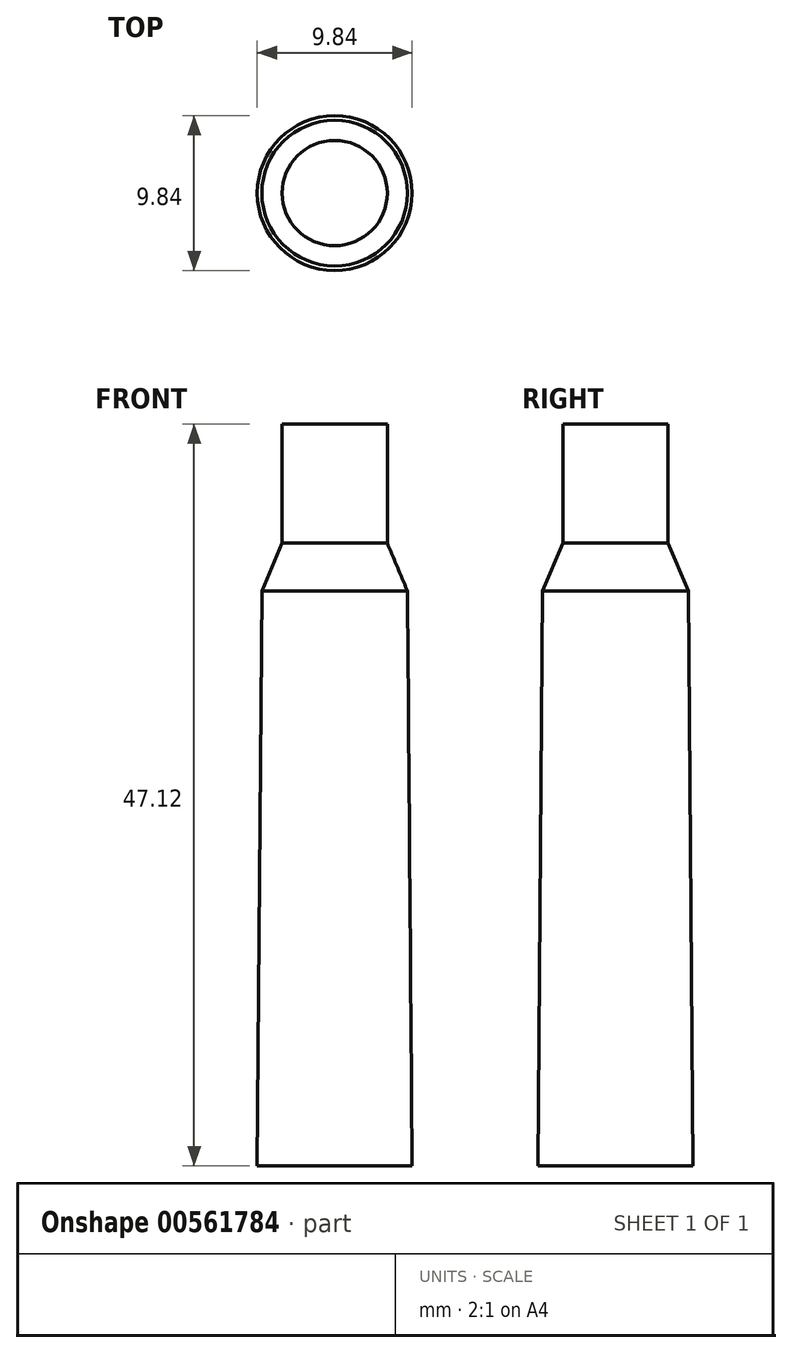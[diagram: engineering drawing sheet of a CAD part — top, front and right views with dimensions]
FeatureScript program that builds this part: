
annotation { "Feature Type Name" : "Feature", "Feature Type Description" : "" }
export const myFeature = defineFeature(function(context is Context, id is Id, definition is map)
    precondition{}
    {
        {
            var Q0;
            Q0=qCreatedBy(makeId("Front.planeOp"),FACE);
            var sketch = newSketch(context, id + "F0", { "sketchPlane" : qUnion([Q0])});
            skLineSegment(sketch, "E0", {"start": v(0, 0) * mm, "end": v(4.92, 0) * mm});
            skLineSegment(sketch, "E1", {"start": v(4.92, 0) * mm, "end": v(4.63, 36.52) * mm});
            skLineSegment(sketch, "E2", {"start": v(4.63, 36.52) * mm, "end": v(0, 36.52) * mm, "construction": true});
            skLineSegment(sketch, "E3", {"start": v(0, 39.55) * mm, "end": v(3.34, 39.55) * mm, "construction": true});
            skLineSegment(sketch, "E4", {"start": v(0, 47.12) * mm, "end": v(3.34, 47.12) * mm});
            skLineSegment(sketch, "E5", {"start": v(3.34, 47.12) * mm, "end": v(3.34, 39.55) * mm});
            skLineSegment(sketch, "E6", {"start": v(4.63, 36.52) * mm, "end": v(3.34, 39.55) * mm});
            skLineSegment(sketch, "E7.MirrorCS", {"start": v(-4.63, 36.52) * mm, "end": v(-3.34, 39.55) * mm});
            skLineSegment(sketch, "E8.MirrorCS", {"start": v(-3.34, 47.12) * mm, "end": v(-3.34, 39.55) * mm});
            skLineSegment(sketch, "E9.MirrorCS", {"start": v(-4.92, 0) * mm, "end": v(-4.63, 36.52) * mm});
            skLineSegment(sketch, "E10", {"start": v(0, 47.12) * mm, "end": v(0, 0) * mm});
            skSolve(sketch);
        }
        {
            var Q0;
            Q0=makeQuery(id+"F0.imprint","IMPRINT",FACE,{"disambiguationData":[TD([[makeQuery(id+"F0.imprint","IMPRINT",EDGE,{"derivedFrom":sQuery(id+"F0.wireOp",EDGE,"E0")}),1.0]])]});
            var Q1;
            Q1=sQuery(id+"F0.wireOp",EDGE,"E10");
            revolve(context, id + "F1", {"entities" : qUnion([Q0]), "axis" : qUnion([Q1]), "revolveType" : RevolveType.FULL});
        }
    });
